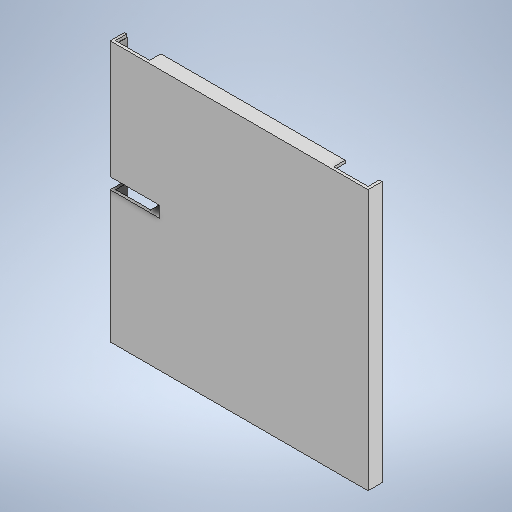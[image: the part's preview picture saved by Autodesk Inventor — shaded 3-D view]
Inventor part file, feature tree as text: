
AUTODESK INVENTOR PART (.ipt)
format: ipt  version: 2025.1 (Build 291241000, 241)  size: 337,408 bytes
history: native  units: mm
features: extrude x8, sketch x5
ambient origin geometry x8: Origin, YZ Plane, XZ Plane, XY Plane, X Axis, Y Axis, Z Axis, Center Point
bodies: Volumenkörper1 (feature_tree)
feature tree (13):
  extrude  "Extrusion1"  Depth=129.4mm
  extrude  "Extrusion2"  Depth=24.75mm
  extrude  "Extrusion3"  Depth=24.75mm
  extrude  "Extrusion4"  Depth=2.0mm TaperAngle=0.0deg
  extrude  "Extrusion5"  Depth=2.0mm
  extrude  "Extrusion6"  Depth=2.0mm
  extrude  "Extrusion7"  Depth=2.0mm
  extrude  "Extrusion17"  Depth=10.0mm TaperAngle=0.0deg
  sketch  "Skizze2"  dims[d0=129.4mm d1=129.4mm]
  sketch  "Skizze4"  dims[d2=22.0mm d3=0.0mm d4=24.75mm]
  sketch  "Skizze6"  dims[d5=24.75mm d6=24.75mm]
  sketch  "Skizze7"  dims[d7=26.75mm d8=2.0mm d9=0.0mm]
  sketch  "Skizze18"  dims[d10=2.0mm d11=2.0mm d12=2.0mm d13=2.0mm d14=10.0mm d15=0.0mm d16=24.5mm d17=24.5mm d18=10.0mm d19=0.0mm d20=27.0mm d21=27.0mm d22=10.0mm d23=0.0mm d26=1.75mm d27=24.25mm d28=1.75mm d29=2.0mm d30=1.75mm d31=2.0mm d32=1.75mm d33=24.25mm d34=2.0mm d35=0.0mm d36=2.0mm d37=0.0mm d97=24.0mm d98=8.0mm d99=35.0mm d100=0.0mm d65=0.5mm d66=0.872665mm d67=0.5mm d68=0.872665mm]
